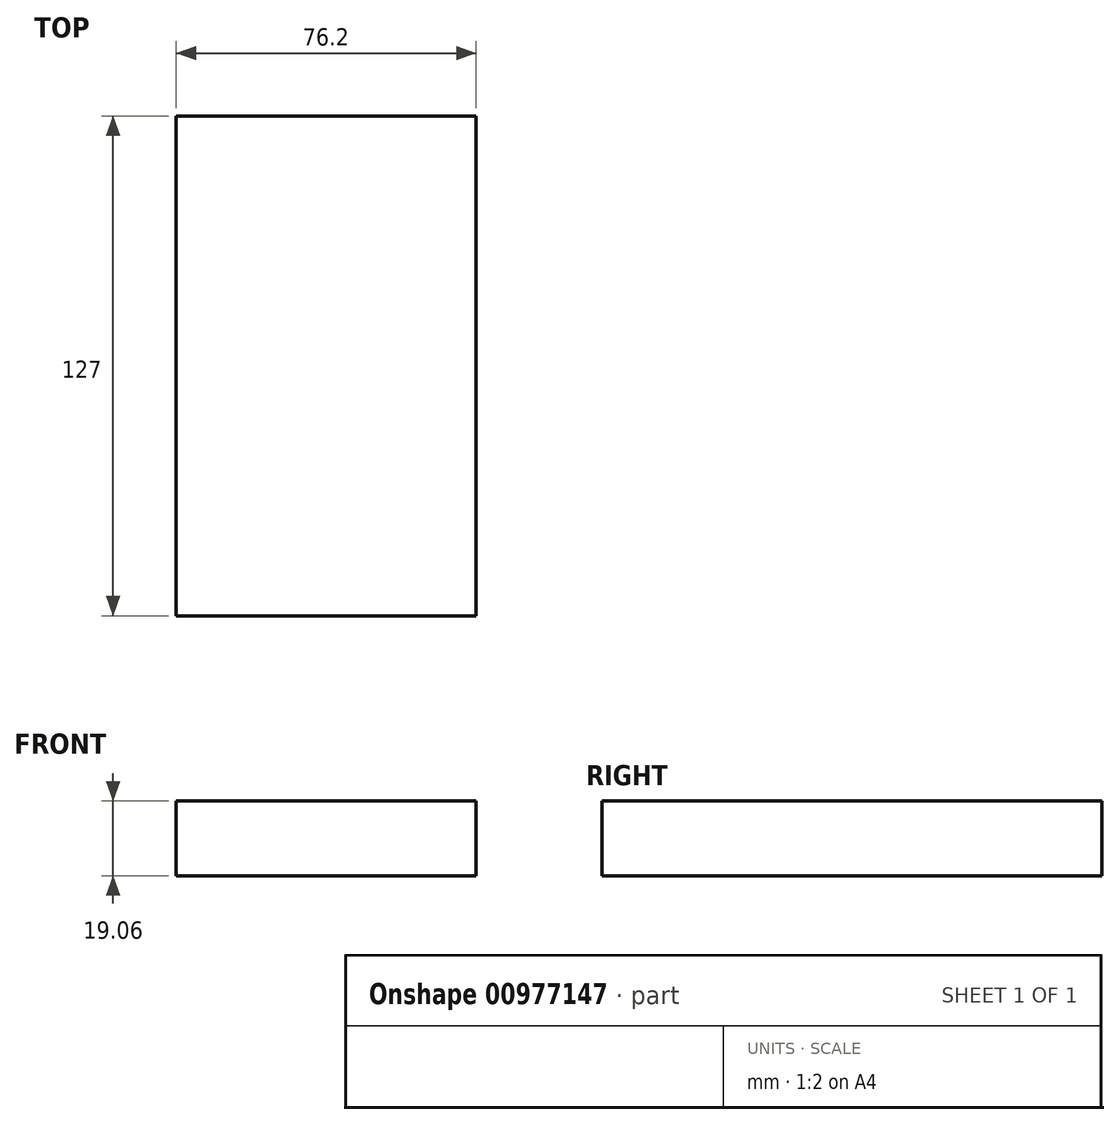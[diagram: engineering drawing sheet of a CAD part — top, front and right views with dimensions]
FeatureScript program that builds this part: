
annotation { "Feature Type Name" : "Feature", "Feature Type Description" : "" }
export const myFeature = defineFeature(function(context is Context, id is Id, definition is map)
    precondition{}
    {
        {
            var Q0;
            Q0=qCreatedBy(makeId("Front.planeOp"),FACE);
            var sketch = newSketch(context, id + "F0", { "sketchPlane" : qUnion([Q0])});
            skLineSegment(sketch, "E0.bottom", {"start": v(-38.1, 9.52) * mm, "end": v(38.1, 9.53) * mm});
            skLineSegment(sketch, "E0.top", {"start": v(-38.1, -9.53) * mm, "end": v(38.1, -9.53) * mm});
            skLineSegment(sketch, "E0.left", {"start": v(-38.1, 9.52) * mm, "end": v(-38.1, -9.53) * mm});
            skLineSegment(sketch, "E0.right", {"start": v(38.1, 9.53) * mm, "end": v(38.1, -9.52) * mm});
            skPoint(sketch, "E0.middle", {"position": v(0, 0) * mm});
            skLineSegment(sketch, "E1.bottom", {"start": v(56.97, 66.67) * mm, "end": v(107.77, 66.67) * mm});
            skLineSegment(sketch, "E1.top", {"start": v(56.97, 38.1) * mm, "end": v(107.77, 38.1) * mm});
            skLineSegment(sketch, "E1.left", {"start": v(56.97, 66.67) * mm, "end": v(56.97, 38.1) * mm});
            skLineSegment(sketch, "E1.right", {"start": v(107.77, 66.67) * mm, "end": v(107.77, 38.1) * mm});
            skPoint(sketch, "E1.middle", {"position": v(82.37, 52.39) * mm});
            skLineSegment(sketch, "E2", {"start": v(38.1, 9.53) * mm, "end": v(38.1, 27) * mm});
            skArc(sketch, "E3", {"start": v(38.1, 27) * mm, "mid": v(42.75, 38.23) * mm, "end": v(53.98, 42.88) * mm});
            skLineSegment(sketch, "E4", {"start": v(53.98, 42.88) * mm, "end": v(82.55, 42.88) * mm});
            skLineSegment(sketch, "E5.0", {"start": v(53.98, 61.93) * mm, "end": v(82.55, 61.93) * mm});
            skArc(sketch, "E5.1", {"start": v(19.05, 27) * mm, "mid": v(29.28, 51.7) * mm, "end": v(53.98, 61.93) * mm});
            skLineSegment(sketch, "E5.2", {"start": v(19.05, 9.53) * mm, "end": v(19.05, 27) * mm});
            skLineSegment(sketch, "E6", {"start": v(82.37, 66.67) * mm, "end": v(82.55, 38.1) * mm});
            skFitSpline(sketch, "E7", {"points": [v(53.98, 61.93) * mm, v(-38.1, 9.53) * mm], "startDerivative": vector(-117.98, 19.66) * mm, "endDerivative": vector(-28.47, -146.97) * mm});
            skSolve(sketch);
        }
        {
            var Q0;
            Q0=makeQuery(id+"F0.imprint","IMPRINT",FACE,{"disambiguationData":[TD([[makeQuery(id+"F0.imprint","IMPRINT",EDGE,{"derivedFrom":sQuery(id+"F0.wireOp",EDGE,"E0.top")}),1.0]])]});
            extrude(context, id + "F1", {"entities" : qUnion([Q0]), "endBound" : BoundingType.SYMMETRIC, "depth" : 127 * mm, "offsetDistance" : 25.4 * mm});
        }
    });
